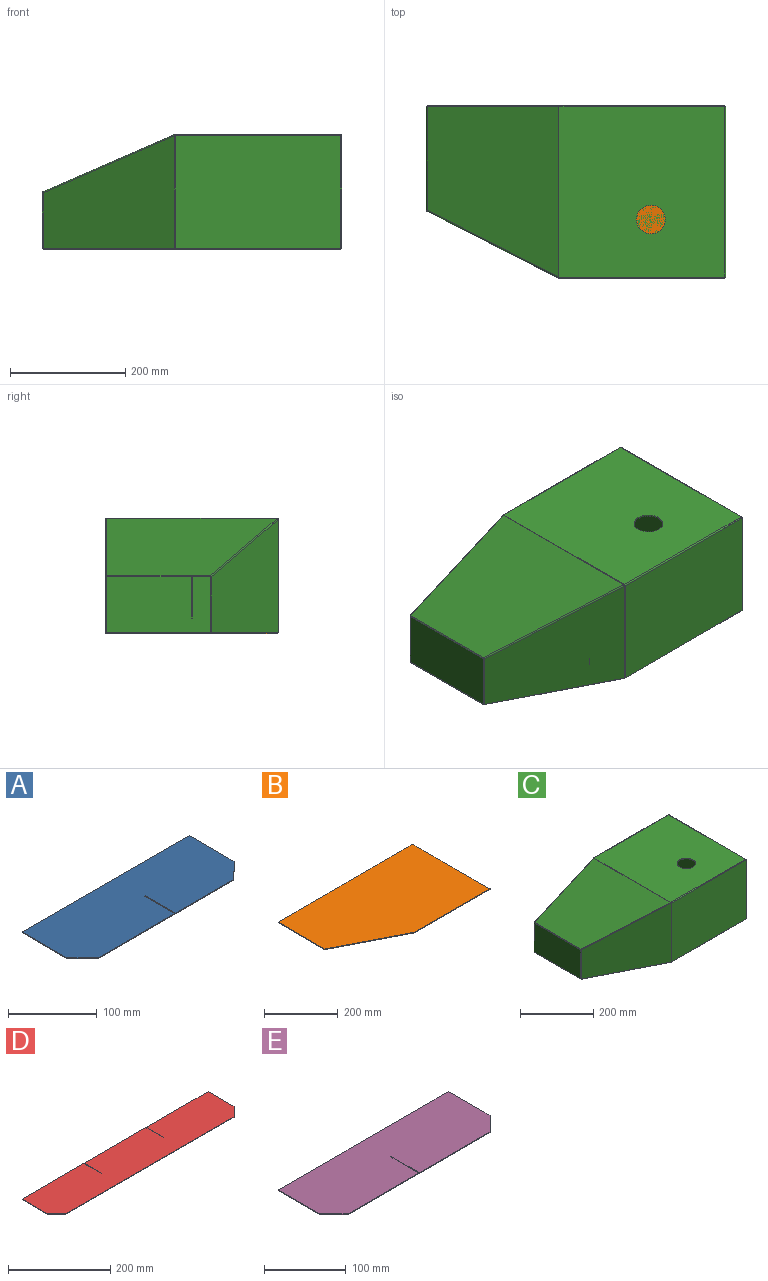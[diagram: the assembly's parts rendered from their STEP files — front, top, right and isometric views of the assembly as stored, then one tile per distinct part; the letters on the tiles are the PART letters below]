
ASSEMBLY  parts=5 mates=12
PART A: 12 faces, bbox 266.9x96.7x1 mm
  f0: plane 71.7x1mm, normal (-1,0,0), area 71.7mm2, adj f1,f9,f10,f11
  f1: plane 25x25mm, normal (-0.71,-0.71,0), area 35.4mm2, adj f0,f2,f10,f11
  f2: plane 122.5x1mm, normal (0,-1,0), area 122.5mm2, adj f1,f3,f10,f11
  f3: plane 48.35x1mm, normal (1,0,0), area 48.4mm2, adj f2,f4,f10,f11
  f4: plane 1x1mm, normal (0,-1,0), area 1mm2, adj f3,f5,f10,f11
  f5: plane 48.35x1mm, normal (-1,0,0), area 48.4mm2, adj f4,f6,f10,f11
  f6: plane 93.4x1mm, normal (0,-1,0), area 93.4mm2, adj f5,f7,f10,f11
  f7: plane 25x25mm, normal (0.71,-0.71,0), area 35.4mm2, adj f6,f8,f10,f11
  f8: plane 71.7x1mm, normal (1,0,0), area 71.7mm2, adj f7,f9,f10,f11
  f9: plane 266.9x1mm, normal (0,1,0), area 266.9mm2, adj f0,f8,f10,f11
  f10: plane 266.9x96.7mm, normal (0,0,1), area 25135.9mm2, adj f0,f1,f2,f3,f4,f5,f6,f7
  f11: plane 266.9x96.7mm, normal (0,0,-1), area 25135.9mm2, adj f0,f1,f2,f3,f4,f5,f6,f7
PART B: 12 faces, bbox 516x296x2 mm
  f0: plane 287.49x2mm, normal (0,-1,0), area 575mm2, adj f1,f9,f10,f11
  f1: cylinder r=0.02mm len=2mm, axis (0,0,-1), area 0.1mm2, adj f0,f2,f10,f11
  f2: plane 295.96x2mm, normal (1,0,0), area 591.9mm2, adj f1,f3,f10,f11
  f3: cylinder r=0.02mm len=2mm, axis (0,0,-1), area 0.1mm2, adj f2,f4,f10,f11
  f4: plane 515.96x2mm, normal (0,1,0), area 1031.9mm2, adj f3,f5,f10,f11
  f5: cylinder r=0.02mm len=2mm, axis (0,0,-1), area 0.1mm2, adj f4,f6,f10,f11
  f6: plane 179.55x2mm, normal (-1,0,0), area 359.1mm2, adj f5,f7,f10,f11
  f7: cylinder r=0.02mm len=2mm, axis (0,0,-1), area 0mm2, adj f6,f8,f10,f11
  f8: plane 228.46x116.41mm, normal (-0.45,-0.89,0), area 512.8mm2, adj f7,f9,f10,f11
  f9: cylinder r=0.04mm len=2mm, axis (0,0,-1), area 0mm2, adj f0,f8,f10,f11
  f10: plane 516x296mm, normal (0,0,1), area 139436.6mm2, adj f0,f1,f2,f3,f4,f5,f6,f7
  f11: plane 516x296mm, normal (0,0,-1), area 139436.6mm2, adj f0,f1,f2,f3,f4,f5,f6,f7
PART C: 76 faces, bbox 520x300x200 mm
  f0: plane 2x0.08mm, normal (0,0,1), area 0.2mm2, adj f4,f5,f6,f58
  f1: plane 2x0.08mm, normal (0,0,1), area 0.2mm2, adj f2,f5,f6,f57
  f2: plane 195.88x2mm, normal (0,-1,0), area 391.8mm2, adj f1,f3,f5,f6
  f3: plane 295.96x2mm, normal (0,0,-1), area 591.9mm2, adj f2,f4,f5,f6
  f4: plane 195.88x2mm, normal (0,1,0), area 391.8mm2, adj f0,f3,f5,f6
  f5: plane 295.96x195.88mm, normal (1,0,0), area 57972.6mm2, adj f0,f1,f2,f3,f4,f59
  f6: plane 295.96x195.88mm, normal (-1,0,0), area 57972.6mm2, adj f0,f1,f2,f3,f4,f60
  f7: plane 2x0.2mm, normal (0,0,1), area 0.4mm2, adj f11,f12,f13,f61
  f8: plane 2x0.08mm, normal (0,0,1), area 0.2mm2, adj f9,f12,f13,f62
  f9: plane 195.8x2mm, normal (1,0,0), area 391.6mm2, adj f8,f12,f13,f72
  f10: plane 96.57x2mm, normal (-1,0,0), area 193.1mm2, adj f11,f12,f13,f71
  f11: plane 228.22x99.23mm, normal (-0.4,0,0.92), area 497.7mm2, adj f7,f10,f12,f13
  f12: plane 515.96x195.8mm, normal (0,1,0), area 89701.9mm2, adj f7,f8,f9,f10,f11,f63,f73
  f13: plane 515.96x195.8mm, normal (0,-1,0), area 89701.9mm2, adj f7,f8,f9,f10,f11,f64,f74
  f14: plane 2x0.05mm, normal (0,-1,0), area 0.1mm2, adj f15,f16,f17,f53
  f15: plane 2x0.03mm, normal (-1,0,0), area 0.1mm2, adj f14,f16,f17,f39
  f16: plane 295.8x287.46mm, normal (0,0,1), area 83068.1mm2, adj f14,f15,f41,f55,f59,f63,f75
  f17: plane 295.8x287.46mm, normal (0,0,-1), area 83068.1mm2, adj f14,f15,f42,f56,f60,f64,f75
  f18: plane 1.82x0.99mm, normal (-0.32,0.16,0.93), area 0.2mm2, adj f19,f23,f24,f43
  f19: plane 195.91x1.78mm, normal (0.89,-0.45,0), area 391.8mm2, adj f18,f22,f23,f24
  f20: plane 1.8x0.95mm, normal (-0.32,0.16,0.93), area 0.1mm2, adj f21,f23,f24,f44
  f21: plane 96.58x1.78mm, normal (-0.89,0.45,0), area 193.2mm2, adj f20,f22,f23,f24
  f22: plane 229.37x118.19mm, normal (0,0,-1), area 512.8mm2, adj f19,f21,f23,f24
  f23: plane 228.46x195.91mm, normal (-0.45,-0.89,0), area 37498.3mm2, adj f18,f19,f20,f21,f22,f45
  f24: plane 228.46x195.91mm, normal (0.45,0.89,0), area 37498.3mm2, adj f18,f19,f20,f21,f22,f46
  f25: plane 1.83x0.8mm, normal (0.92,0,0.4), area 0.2mm2, adj f26,f27,f28,f40
  f26: plane 229.13x101.12mm, normal (0,1,0), area 498mm2, adj f25,f27,f28,f36
  f27: plane 295.85x228.34mm, normal (-0.4,0,0.92), area 59177.9mm2, adj f25,f26,f37,f41,f45
  f28: plane 295.85x228.34mm, normal (0.4,0,-0.92), area 59177.9mm2, adj f25,f26,f38,f42,f46
  f29: plane 2x0.05mm, normal (0,0,1), area 0.1mm2, adj f32,f33,f34,f35
  f30: plane 96.6x2mm, normal (0,1,0), area 193.2mm2, adj f31,f33,f34,f36
  f31: plane 179.55x2mm, normal (0,0,-1), area 359.1mm2, adj f30,f32,f33,f34
  f32: plane 96.6x2mm, normal (0,-1,0), area 193.2mm2, adj f29,f31,f33,f34
  f33: plane 179.55x96.6mm, normal (-1,0,0), area 17343.9mm2, adj f29,f30,f31,f32,f37
  f34: plane 179.55x96.6mm, normal (1,0,0), area 17343.9mm2, adj f29,f30,f31,f32,f38
  f35: plane 2.06x1.93mm, normal (0,-1,0), area 2.6mm2, adj f29,f37,f38,f44
  f36: plane 2.06x1.93mm, normal (0,1,0), area 2.6mm2, adj f26,f30,f37,f38
  f37: cylinder r=2.1mm len=179.5mm, axis (0,-1,0), area 437.5mm2, adj f27,f33,f35,f36
  f38: cylinder r=0.1mm len=179.5mm, axis (0,-1,0), area 20.8mm2, adj f28,f34,f35,f36
  f39: plane 2.01x0.84mm, normal (0,-1,0), area 0.9mm2, adj f15,f41,f42,f43
  f40: plane 2.01x0.84mm, normal (0,1,0), area 0.9mm2, adj f25,f41,f42,f61
  f41: cylinder r=2.1mm len=295.77mm, axis (0,-1,0), area 254.7mm2, adj f16,f27,f39,f40
  f42: cylinder r=0.1mm len=295.77mm, axis (0,-1,0), area 12.1mm2, adj f17,f28,f39,f40
  f43: plane 1.93x1.87mm, normal (0.83,-0.42,0.36), area 3.1mm2, adj f18,f39,f45,f46
  f44: plane 1.93x1.87mm, normal (-0.83,0.42,-0.36), area 3.1mm2, adj f20,f35,f45,f46
  f45: cylinder r=2.1mm len=228.67mm, axis (0.83,-0.42,0.36), area 801.5mm2, adj f23,f27,f43,f44
  f46: cylinder r=0.1mm len=228.35mm, axis (0.83,-0.42,0.36), area 38.2mm2, adj f24,f28,f43,f44
  f47: plane 2x0.08mm, normal (0,0,1), area 0.2mm2, adj f49,f51,f52,f54
  f48: plane 287.49x2mm, normal (0,0,-1), area 575mm2, adj f49,f50,f51,f52
  f49: plane 195.88x2mm, normal (1,0,0), area 391.8mm2, adj f47,f48,f51,f52
  f50: plane 195.88x2mm, normal (-1,0,0), area 391.8mm2, adj f48,f51,f52,f53
  f51: plane 287.49x195.88mm, normal (0,-1,0), area 56313.4mm2, adj f47,f48,f49,f50,f55
  f52: plane 287.49x195.88mm, normal (0,1,0), area 56313.4mm2, adj f47,f48,f49,f50,f56
  f53: plane 2.1x2.1mm, normal (-1,0,0), area 3.5mm2, adj f14,f50,f55,f56
  f54: plane 2.1x2.1mm, normal (1,0,0), area 3.5mm2, adj f47,f55,f56,f57
  f55: cylinder r=2.1mm len=287.41mm, axis (-1,0,0), area 948.1mm2, adj f16,f51,f53,f54
  f56: cylinder r=0.1mm len=287.41mm, axis (-1,0,0), area 45.1mm2, adj f17,f52,f53,f54
  f57: plane 2.1x2.1mm, normal (0,-1,0), area 3.5mm2, adj f1,f54,f59,f60
  f58: plane 2.1x2.1mm, normal (0,1,0), area 3.5mm2, adj f0,f59,f60,f62
  f59: cylinder r=2.1mm len=295.8mm, axis (0,-1,0), area 975.7mm2, adj f5,f16,f57,f58
  f60: cylinder r=0.1mm len=295.8mm, axis (0,-1,0), area 46.5mm2, adj f6,f17,f57,f58
  f61: plane 2.1x2.1mm, normal (-1,0,0), area 3.5mm2, adj f7,f40,f63,f64
  f62: plane 2.1x2.1mm, normal (1,0,0), area 3.5mm2, adj f8,f58,f63,f64
  f63: cylinder r=2.1mm len=287.46mm, axis (-1,0,0), area 948.2mm2, adj f12,f16,f61,f62
  f64: cylinder r=0.1mm len=287.46mm, axis (-1,0,0), area 45.2mm2, adj f13,f17,f61,f62
  f65: plane 179.47x2mm, normal (-1,0,0), area 358.9mm2, adj f68,f69,f70,f71
  f66: plane 295.88x2mm, normal (1,0,0), area 591.8mm2, adj f67,f69,f70,f72
  f67: plane 287.5x2mm, normal (0,-1,0), area 575mm2, adj f66,f68,f69,f70
  f68: plane 228.47x116.41mm, normal (-0.45,-0.89,0), area 512.8mm2, adj f65,f67,f69,f70
  f69: plane 515.96x295.88mm, normal (0,0,-1), area 139364.6mm2, adj f65,f66,f67,f68,f73
  f70: plane 515.96x295.88mm, normal (0,0,1), area 139364.6mm2, adj f65,f66,f67,f68,f74
  f71: plane 2.1x2.1mm, normal (-1,0,0), area 3.5mm2, adj f10,f65,f73,f74
  f72: plane 2.1x2.1mm, normal (1,0,0), area 3.5mm2, adj f9,f66,f73,f74
  f73: cylinder r=2.1mm len=515.96mm, axis (-1,0,0), area 1702mm2, adj f12,f69,f71,f72
  f74: cylinder r=0.1mm len=515.96mm, axis (-1,0,0), area 81mm2, adj f13,f70,f71,f72
  f75: cylinder r=25mm len=50mm, axis (0,0,1), area 314.2mm2, adj f16,f17
PART D: 16 faces, bbox 516x96.7x1 mm
  f0: plane 48.35x1mm, normal (1,0,0), area 48.3mm2, adj f1,f13,f14,f15
  f1: plane 171.33x1mm, normal (0,1,0), area 171.3mm2, adj f0,f2,f14,f15
  f2: plane 71.7x1mm, normal (-1,0,0), area 71.7mm2, adj f1,f3,f14,f15
  f3: plane 25x25mm, normal (-0.71,-0.71,0), area 35.4mm2, adj f2,f4,f14,f15
  f4: plane 466x1mm, normal (0,-1,0), area 466mm2, adj f3,f5,f14,f15
  f5: plane 25x25mm, normal (0.71,-0.71,0), area 35.4mm2, adj f4,f6,f14,f15
  f6: plane 71.7x1mm, normal (1,0,0), area 71.7mm2, adj f5,f7,f14,f15
  f7: plane 171.33x1mm, normal (0,1,0), area 171.3mm2, adj f6,f8,f14,f15
  f8: plane 48.35x1mm, normal (-1,0,0), area 48.3mm2, adj f7,f9,f14,f15
  f9: plane 1x1mm, normal (0,1,0), area 1mm2, adj f8,f10,f14,f15
  f10: plane 48.35x1mm, normal (1,0,0), area 48.3mm2, adj f9,f11,f14,f15
  f11: plane 171.33x1mm, normal (0,1,0), area 171.3mm2, adj f10,f12,f14,f15
  f12: plane 48.35x1mm, normal (-1,0,0), area 48.3mm2, adj f11,f13,f14,f15
  f13: plane 1x1mm, normal (0,1,0), area 1mm2, adj f0,f12,f14,f15
  f14: plane 516x96.7mm, normal (0,0,1), area 49175.5mm2, adj f0,f1,f2,f3,f4,f5,f6,f7
  f15: plane 516x96.7mm, normal (0,0,-1), area 49175.5mm2, adj f0,f1,f2,f3,f4,f5,f6,f7
PART E: 12 faces, bbox 296x96.7x1 mm
  f0: plane 71.7x1mm, normal (-1,0,0), area 71.7mm2, adj f1,f9,f10,f11
  f1: plane 25x25mm, normal (-0.71,-0.71,0), area 35.4mm2, adj f0,f2,f10,f11
  f2: plane 122.5x1mm, normal (0,-1,0), area 122.5mm2, adj f1,f3,f10,f11
  f3: plane 48.35x1mm, normal (1,0,0), area 48.4mm2, adj f2,f4,f10,f11
  f4: plane 1x1mm, normal (0,-1,0), area 1mm2, adj f3,f5,f10,f11
  f5: plane 48.35x1mm, normal (-1,0,0), area 48.4mm2, adj f4,f6,f10,f11
  f6: plane 122.5x1mm, normal (0,-1,0), area 122.5mm2, adj f5,f7,f10,f11
  f7: plane 25x25mm, normal (0.71,-0.71,0), area 35.4mm2, adj f6,f8,f10,f11
  f8: plane 71.7x1mm, normal (1,0,0), area 71.7mm2, adj f7,f9,f10,f11
  f9: plane 296x1mm, normal (0,1,0), area 296mm2, adj f0,f8,f10,f11
  f10: plane 296x96.7mm, normal (0,0,1), area 27949.8mm2, adj f0,f1,f2,f3,f4,f5,f6,f7
  f11: plane 296x96.7mm, normal (0,0,-1), area 27949.8mm2, adj f0,f1,f2,f3,f4,f5,f6,f7
PLACE A rot(axis=(0.58,-0.58,-0.58),120deg) t=(-85.67,148,215.4)mm
PLACE B rot(axis=(1,0,0),0deg) t=(0,0,0)mm
PLACE C at identity fixed
PLACE D rot(axis=(0,0.71,0.71),180deg) t=(258,-0.5,2)mm
PLACE E rot(axis=(0.58,-0.58,-0.58),120deg) t=(86.67,148,108.7)mm
MATE planar A.f9 <-> D.f11  axis (0,0,1) through (-86.17,14.55,98.7)mm
MATE planar B.f6 <-> C.f34  axis (-1,0,0) through (-258,58.21,1)mm
MATE planar A.f3 <-> D.f14  axis (0,-1,0) through (-86.17,0.5,26.17)mm
MATE planar B.f4 <-> C.f13  axis (0,1,0) through (0,148,1)mm
MATE planar D.f2 <-> C.f6  axis (1,0,0) through (258,0,62.85)mm
MATE planar D.f4 <-> B.f10  axis (0,0,-1) through (0,0,2)mm
MATE planar D.f9 <-> E.f4  axis (0,0,1) through (-86.17,0,50.35)mm
MATE planar D.f0 <-> E.f11  axis (-1,0,0) through (86.67,0,74.52)mm
MATE planar E.f8 <-> C.f52  axis (0,-1,0) through (86.17,-148,62.85)mm
MATE planar A.f10 <-> D.f8  axis (-1,0,0) through (-86.67,0,50.35)mm
MATE planar E.f2 <-> D.f4  axis (0,0,-1) through (86.17,61.75,2)mm
MATE planar B.f10 <-> D.f4  axis (0,0,1) through (17.34,10.41,2)mm
